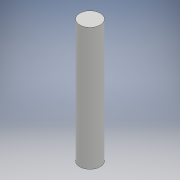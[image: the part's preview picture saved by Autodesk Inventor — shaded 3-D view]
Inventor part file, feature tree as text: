
AUTODESK INVENTOR PART (.ipt)
format: ipt  version: 2018 (Build 220112000, 112)  size: 90,112 bytes
history: native  units: mm
features: other x1, extrude x1, sketch x1
ambient origin geometry x8: Origin, YZ Plane, XZ Plane, XY Plane, X Axis, Y Axis, Z Axis, Center Point
bodies: Body1 (feature_tree)
feature tree (3):
  other  "Твердое тело1"
  extrude  "Выдавливание1"  Depth=5.0mm
  sketch  "Эскиз1"
